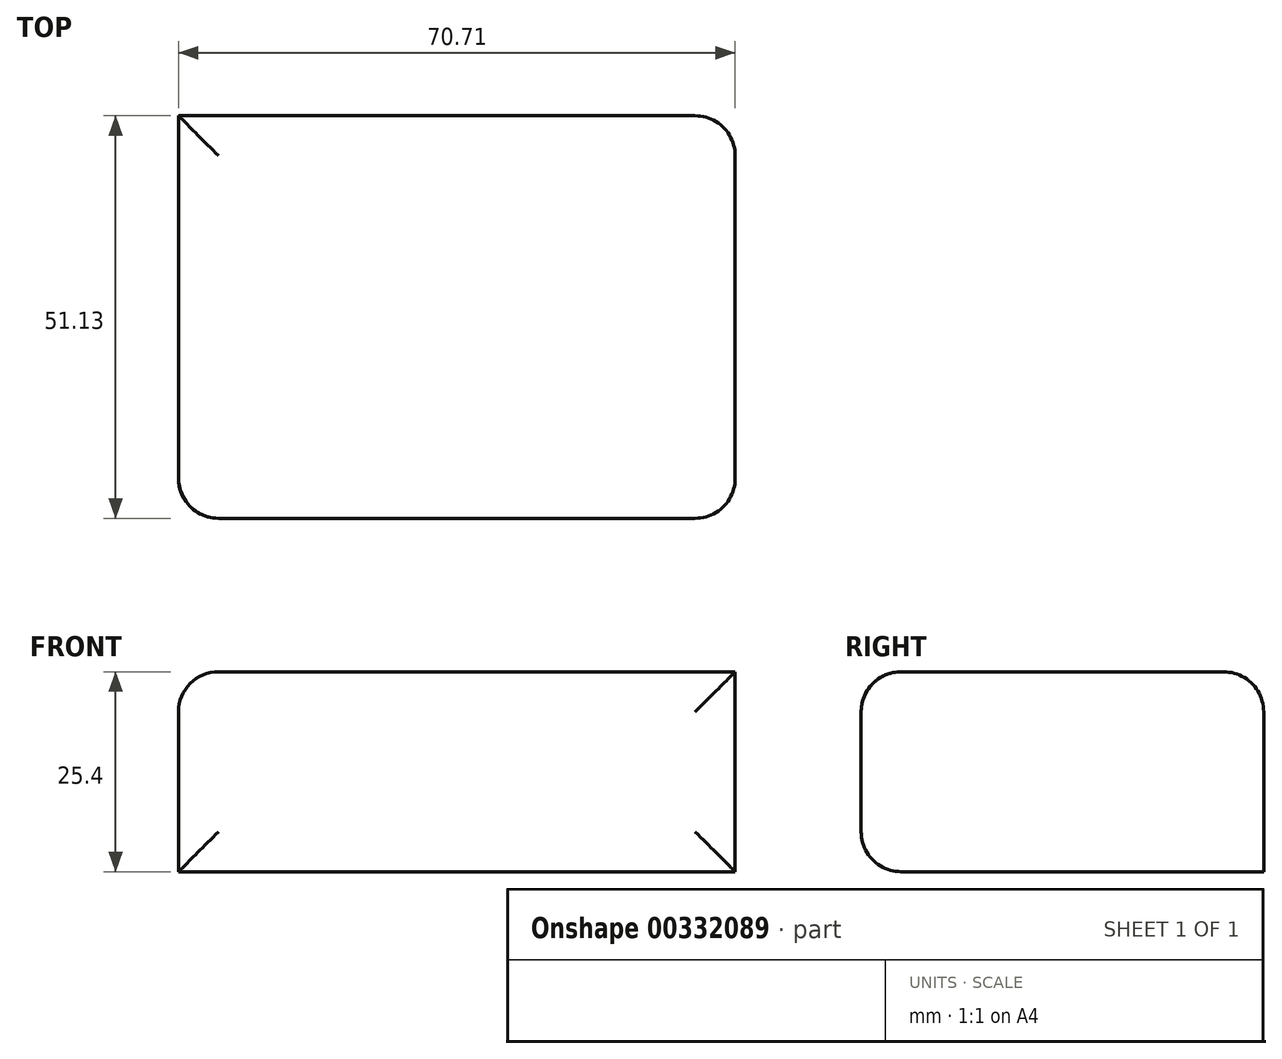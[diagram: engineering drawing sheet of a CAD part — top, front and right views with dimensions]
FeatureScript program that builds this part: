
annotation { "Feature Type Name" : "Feature", "Feature Type Description" : "" }
export const myFeature = defineFeature(function(context is Context, id is Id, definition is map)
    precondition{}
    {
        {
            var Q0;
            Q0=qCreatedBy(makeId("Top.planeOp"),FACE);
            var sketch = newSketch(context, id + "F0", { "sketchPlane" : qUnion([Q0])});
            skLineSegment(sketch, "E0.bottom", {"start": v(-46.78, -26.53) * mm, "end": v(23.93, -26.53) * mm});
            skLineSegment(sketch, "E0.top", {"start": v(-46.78, 24.6) * mm, "end": v(23.93, 24.6) * mm});
            skLineSegment(sketch, "E0.left", {"start": v(-46.78, -26.53) * mm, "end": v(-46.78, 24.6) * mm});
            skLineSegment(sketch, "E0.right", {"start": v(23.93, -26.53) * mm, "end": v(23.93, 24.6) * mm});
            skSolve(sketch);
        }
        {
            var Q0;
            Q0=makeQuery(id+"F0.imprint","IMPRINT",FACE,{"disambiguationData":[TD([[makeQuery(id+"F0.imprint","IMPRINT",EDGE,{"derivedFrom":sQuery(id+"F0.wireOp",EDGE,"E0.bottom")}),1.0]])]});
            extrude(context, id + "F1", {"entities" : qUnion([Q0]), "depth" : 25.4 * mm});
        }
        {
            var Q0;
            Q0=makeQuery(id+"F1.opExtrude","SWEPT_FACE",FACE,{"disambiguationData":[OSD([sQuery(id+"F0.wireOp",EDGE,"E0.bottom")])]});
            var Q1;
            Q1=makeQuery(id+"F1.opExtrude","CAP_EDGE",EDGE,{"disambiguationData":[OSD([sQuery(id+"F0.wireOp",EDGE,"E0.top")])],"isStart":false});
            var Q2;
            Q2=makeQuery(id+"F1.opExtrude","SWEPT_EDGE",EDGE,{"disambiguationData":[OSD([sQuery(id+"F0.wireOp",EDGE,"E0.top"),sQuery(id+"F0.wireOp",EDGE,"E0.right")])]});
            var Q3;
            Q3=makeQuery(id+"F1.opExtrude","CAP_EDGE",EDGE,{"disambiguationData":[OSD([sQuery(id+"F0.wireOp",EDGE,"E0.left")])],"isStart":false});
            fillet(context, id + "F2", {"entities" : qUnion([Q0, Q1, Q2, Q3]), "radius" : 5.08 * mm, "tangentPropagation" : true, "allowEdgeOverflow" : false});
        }
    });
